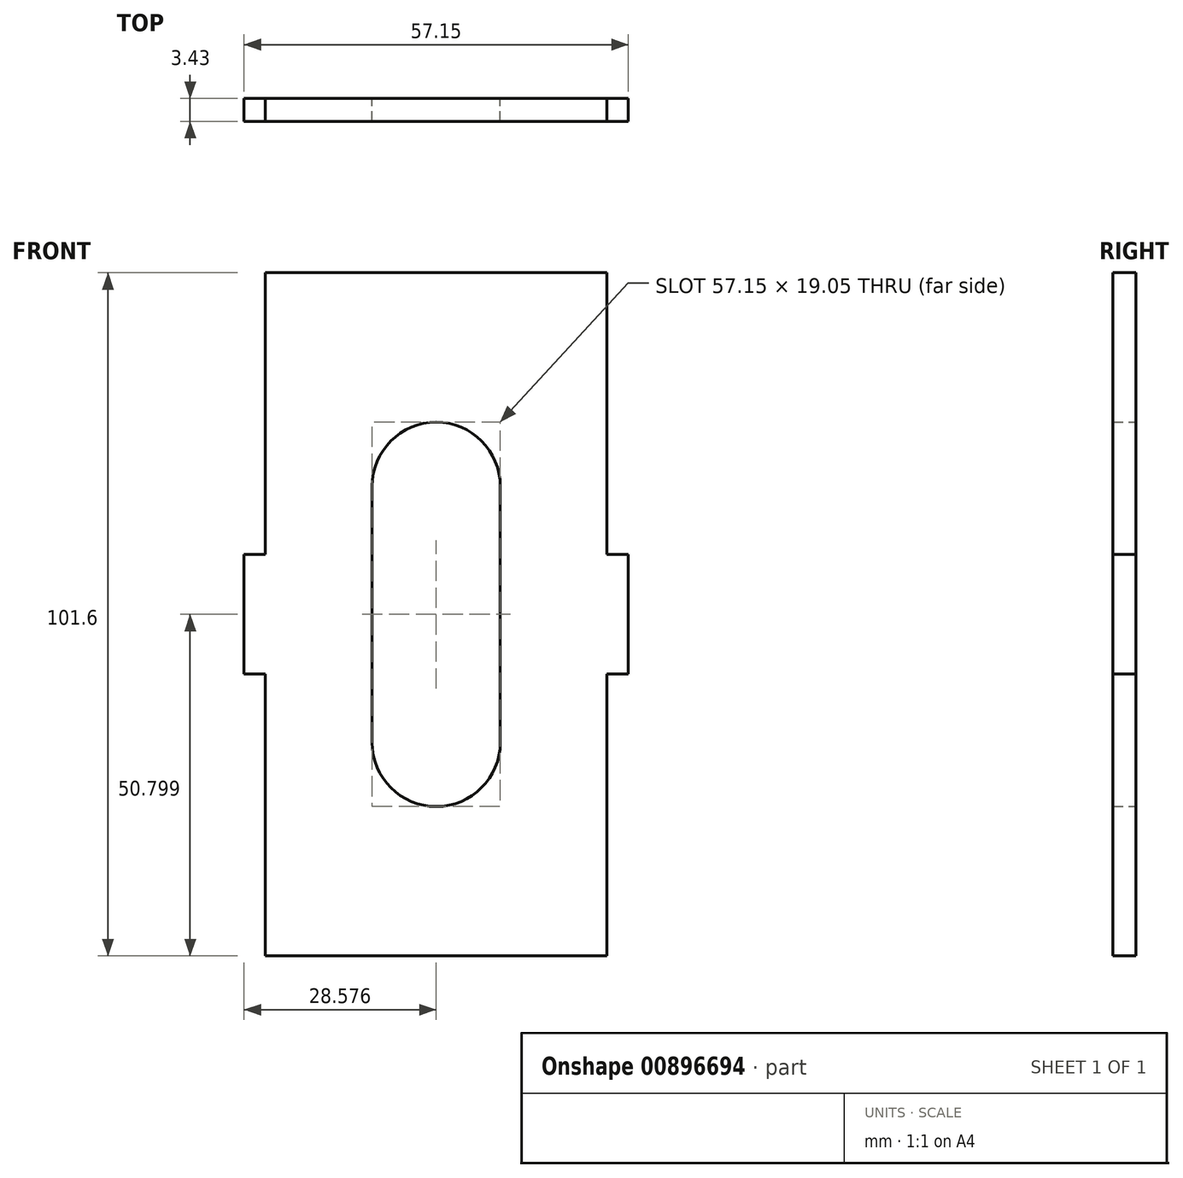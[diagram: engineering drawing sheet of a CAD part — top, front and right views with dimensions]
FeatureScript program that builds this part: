
annotation { "Feature Type Name" : "Feature", "Feature Type Description" : "" }
export const myFeature = defineFeature(function(context is Context, id is Id, definition is map)
    precondition{}
    {
        {
            var Q0;
            Q0=qCreatedBy(makeId("Front.planeOp"),FACE);
            var sketch = newSketch(context, id + "F0", { "sketchPlane" : qUnion([Q0])});
            skLineSegment(sketch, "E0", {"start": v(-594.65, 433.75) * mm, "end": v(-594.65, 471.85) * mm});
            skArc(sketch, "E1", {"start": v(-594.65, 471.85) * mm, "mid": v(-604.17, 481.37) * mm, "end": v(-613.7, 471.85) * mm});
            skLineSegment(sketch, "E2", {"start": v(-613.7, 471.85) * mm, "end": v(-613.7, 433.75) * mm});
            skArc(sketch, "E3", {"start": v(-613.7, 433.75) * mm, "mid": v(-604.17, 424.22) * mm, "end": v(-594.65, 433.75) * mm});
            skLineSegment(sketch, "E4", {"start": v(-575.6, 461.69) * mm, "end": v(-578.77, 461.69) * mm});
            skLineSegment(sketch, "E5", {"start": v(-575.6, 443.9) * mm, "end": v(-575.6, 461.69) * mm});
            skLineSegment(sketch, "E6", {"start": v(-578.77, 443.9) * mm, "end": v(-575.6, 443.9) * mm});
            skLineSegment(sketch, "E7", {"start": v(-578.77, 402) * mm, "end": v(-578.77, 443.9) * mm});
            skLineSegment(sketch, "E8", {"start": v(-629.57, 402) * mm, "end": v(-578.77, 402) * mm});
            skLineSegment(sketch, "E9", {"start": v(-629.57, 443.9) * mm, "end": v(-629.57, 402) * mm});
            skLineSegment(sketch, "E10", {"start": v(-632.75, 443.9) * mm, "end": v(-629.57, 443.9) * mm});
            skLineSegment(sketch, "E11", {"start": v(-632.75, 461.69) * mm, "end": v(-632.75, 443.9) * mm});
            skLineSegment(sketch, "E12", {"start": v(-629.57, 461.69) * mm, "end": v(-632.75, 461.69) * mm});
            skLineSegment(sketch, "E13", {"start": v(-629.57, 503.6) * mm, "end": v(-629.57, 461.69) * mm});
            skLineSegment(sketch, "E14", {"start": v(-578.77, 503.6) * mm, "end": v(-629.57, 503.6) * mm});
            skLineSegment(sketch, "E15", {"start": v(-578.77, 461.69) * mm, "end": v(-578.77, 503.6) * mm});
            skSolve(sketch);
        }
        {
            var Q0;
            Q0 = qSketchRegion(id + "F0", true);
            extrude(context, id + "F1", {"entities" : qUnion([Q0]), "depth" : 3.43 * mm, "offsetDistance" : 25.4 * mm});
        }
    });
